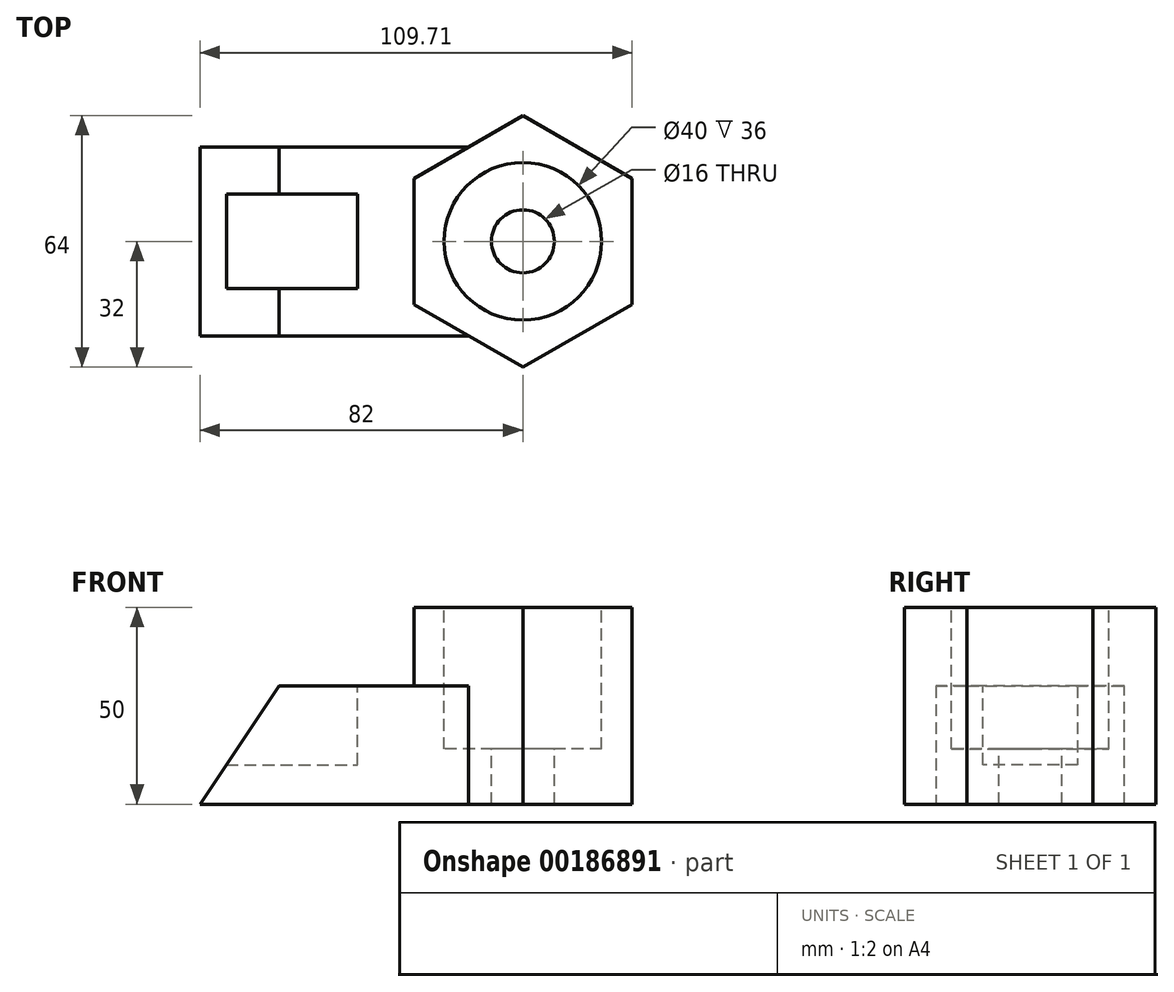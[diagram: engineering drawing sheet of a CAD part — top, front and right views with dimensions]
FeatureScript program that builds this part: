
annotation { "Feature Type Name" : "Feature", "Feature Type Description" : "" }
export const myFeature = defineFeature(function(context is Context, id is Id, definition is map)
    precondition{}
    {
        {
            var Q0;
            Q0=qCreatedBy(makeId("Top.planeOp"),FACE);
            var sketch = newSketch(context, id + "F0", { "sketchPlane" : qUnion([Q0])});
            skCircle(sketch, "E0.cCircle", {"center": v(0, 0) * mm, "radius": 27.71 * mm, "construction": true});
            skLineSegment(sketch, "E0.0", {"start": v(0, 32) * mm, "end": v(27.71, 16) * mm});
            skLineSegment(sketch, "E0.1", {"start": v(27.71, 16) * mm, "end": v(27.71, -16) * mm});
            skLineSegment(sketch, "E0.2", {"start": v(27.71, -16) * mm, "end": v(0, -32) * mm});
            skLineSegment(sketch, "E0.3", {"start": v(0, -32) * mm, "end": v(-27.71, -16) * mm});
            skLineSegment(sketch, "E0.4", {"start": v(-27.71, -16) * mm, "end": v(-27.71, 16) * mm});
            skLineSegment(sketch, "E0.5", {"start": v(-27.71, 16) * mm, "end": v(0, 32) * mm});
            skPoint(sketch, "E0.0.midPoint", {"position": v(13.86, 24) * mm});
            skLineSegment(sketch, "E1", {"start": v(-13.86, -24) * mm, "end": v(-82, -24) * mm});
            skLineSegment(sketch, "E2", {"start": v(-82, -24) * mm, "end": v(-82, 24) * mm});
            skLineSegment(sketch, "E3", {"start": v(-82, 24) * mm, "end": v(-13.86, 24) * mm});
            skSolve(sketch);
        }
        {
            var Q0;
            {var subQ2=sQuery(id+"F0.wireOp",EDGE,"E0.4");Q0=makeQuery(id+"F0.imprint","IMPRINT",FACE,{"disambiguationData":[TD([[makeQuery(id+"F0.imprint","IMPRINT",EDGE,{"derivedFrom":subQ2}),1.0]])]});}
            extrude(context, id + "F1", {"entities" : qUnion([Q0]), "depth" : 30 * mm});
        }
        {
            var Q0;
            {var subQ3=sQuery(id+"F0.wireOp",EDGE,"E0.0");Q0=makeQuery(id+"F0.imprint","IMPRINT",FACE,{"disambiguationData":[TD([[makeQuery(id+"F0.imprint","IMPRINT",EDGE,{"derivedFrom":subQ3}),-1.0]])]});}
            extrude(context, id + "F2", {"entities" : qUnion([Q0]), "operationType" : NewBodyOperationType.ADD, "depth" : 50 * mm});
        }
        {
            var Q0;
            Q0=makeQuery(id+"F2.opExtrude","CAP_FACE",FACE,{"disambiguationData":[OSD([sQuery(id+"F0.wireOp",EDGE,"E0.0"),sQuery(id+"F0.wireOp",EDGE,"E0.1"),sQuery(id+"F0.wireOp",EDGE,"E0.2"),sQuery(id+"F0.wireOp",EDGE,"E0.3"),sQuery(id+"F0.wireOp",EDGE,"E0.4"),sQuery(id+"F0.wireOp",EDGE,"E0.5")])],"isStart":false});
            var sketch = newSketch(context, id + "F3", { "sketchPlane" : qUnion([Q0])});
            skCircle(sketch, "E4", {"center": v(0, 0) * mm, "radius": 20 * mm});
            skSolve(sketch);
        }
        {
            var Q0;
            Q0=makeQuery(id+"F3.imprint","IMPRINT",FACE,{"disambiguationData":[TD([[makeQuery(id+"F3.imprint","IMPRINT",EDGE,{"derivedFrom":sQuery(id+"F3.wireOp",EDGE,"E4")}),1.0]])]});
            extrude(context, id + "F4", {"entities" : qUnion([Q0]), "operationType" : NewBodyOperationType.REMOVE, "oppositeDirection" : true, "depth" : 36 * mm});
        }
        {
            var Q0;
            Q0=makeQuery(id+"F4.boolean.opBoolean","COPY",FACE,{"derivedFrom":makeQuery(id+"F4.opExtrude","CAP_FACE",FACE,{"disambiguationData":[OSD([sQuery(id+"F3.wireOp",EDGE,"E4")])],"isStart":false})});
            var sketch = newSketch(context, id + "F5", { "sketchPlane" : qUnion([Q0])});
            skCircle(sketch, "E5", {"center": v(0, 0) * mm, "radius": 8 * mm});
            skSolve(sketch);
        }
        {
            var Q0;
            Q0=makeQuery(id+"F5.imprint","IMPRINT",FACE,{"disambiguationData":[TD([[makeQuery(id+"F5.imprint","IMPRINT",EDGE,{"derivedFrom":sQuery(id+"F5.wireOp",EDGE,"E5")}),1.0]])]});
            extrude(context, id + "F6", {"entities" : qUnion([Q0]), "operationType" : NewBodyOperationType.REMOVE, "endBound" : BoundingType.THROUGH_ALL, "oppositeDirection" : true, "depth" : 25 * mm});
        }
        {
            var Q0;
            Q0=makeQuery(id+"F1.opExtrude","CAP_FACE",FACE,{"disambiguationData":[OSD([sQuery(id+"F0.wireOp",EDGE,"E0.3"),sQuery(id+"F0.wireOp",EDGE,"E0.4"),sQuery(id+"F0.wireOp",EDGE,"E0.5"),sQuery(id+"F0.wireOp",EDGE,"E1"),sQuery(id+"F0.wireOp",EDGE,"E2"),sQuery(id+"F0.wireOp",EDGE,"E3")])],"isStart":false});
            var sketch = newSketch(context, id + "F7", { "sketchPlane" : qUnion([Q0])});
            skLineSegment(sketch, "E6", {"start": v(-82, 12) * mm, "end": v(-42, 12) * mm});
            skLineSegment(sketch, "E7", {"start": v(-42, 12) * mm, "end": v(-42, -12) * mm});
            skLineSegment(sketch, "E8", {"start": v(-42, -12) * mm, "end": v(-82, -12) * mm});
            skLineSegment(sketch, "E9", {"start": v(-82, 12) * mm, "end": v(-82, -12) * mm});
            skLineSegment(sketch, "E10", {"start": v(-82, 24) * mm, "end": v(-82, 12) * mm, "construction": true});
            skLineSegment(sketch, "E11", {"start": v(-82, -12) * mm, "end": v(-82, -24) * mm, "construction": true});
            skSolve(sketch);
        }
        {
            var Q0;
            Q0=makeQuery(id+"F7.imprint","IMPRINT",FACE,{"disambiguationData":[TD([[makeQuery(id+"F7.imprint","IMPRINT",EDGE,{"derivedFrom":sQuery(id+"F7.wireOp",EDGE,"E6")}),-1.0]])]});
            extrude(context, id + "F8", {"entities" : qUnion([Q0]), "operationType" : NewBodyOperationType.REMOVE, "oppositeDirection" : true, "depth" : 20 * mm});
        }
        {
            var Q0;
            Q0=makeQuery(id+"F1.opExtrude","SWEPT_FACE",FACE,{"disambiguationData":[OSD([sQuery(id+"F0.wireOp",EDGE,"E1")])]});
            var sketch = newSketch(context, id + "F9", { "sketchPlane" : qUnion([Q0])});
            skLineSegment(sketch, "E12", {"start": v(-82, 0) * mm, "end": v(-82, 30) * mm});
            skLineSegment(sketch, "E13", {"start": v(-82, 30) * mm, "end": v(-62, 30) * mm});
            skLineSegment(sketch, "E14", {"start": v(-62, 30) * mm, "end": v(-82, 0) * mm});
            skSolve(sketch);
        }
        {
            var Q0;
            Q0=makeQuery(id+"F9.imprint","IMPRINT",FACE,{"disambiguationData":[TD([[makeQuery(id+"F9.imprint","IMPRINT",EDGE,{"derivedFrom":sQuery(id+"F9.wireOp",EDGE,"E12")}),1.0]])]});
            extrude(context, id + "F10", {"entities" : qUnion([Q0]), "operationType" : NewBodyOperationType.REMOVE, "endBound" : BoundingType.THROUGH_ALL, "oppositeDirection" : true, "depth" : 25 * mm});
        }
    });
